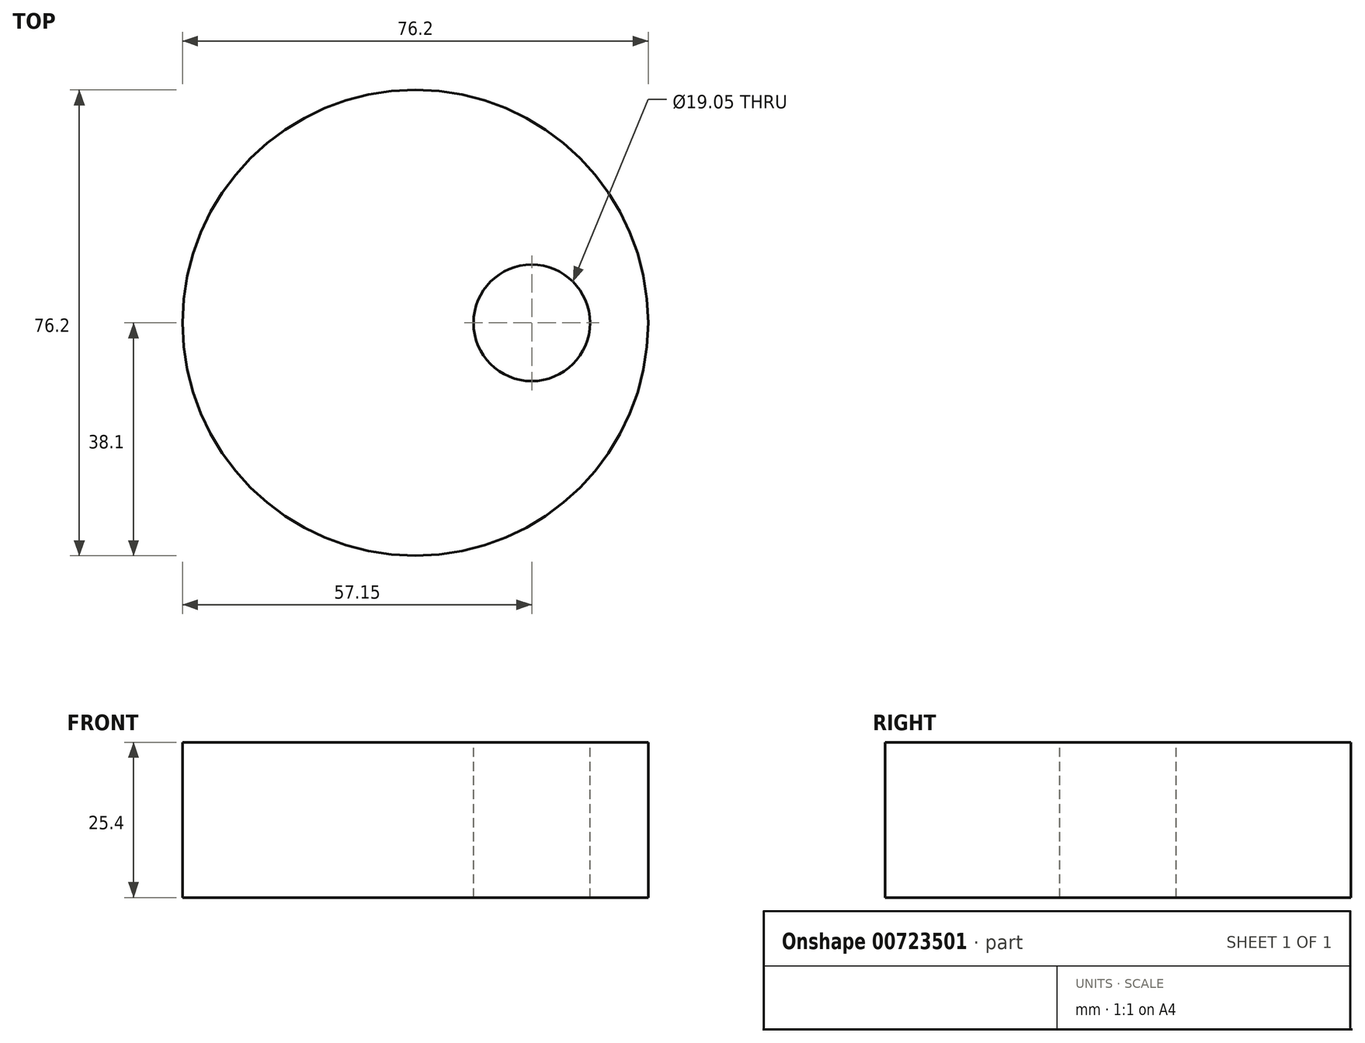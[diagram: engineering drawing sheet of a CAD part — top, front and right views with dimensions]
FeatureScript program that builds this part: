
annotation { "Feature Type Name" : "Feature", "Feature Type Description" : "" }
export const myFeature = defineFeature(function(context is Context, id is Id, definition is map)
    precondition{}
    {
        {
            var Q0;
            Q0=qCreatedBy(makeId("Top.planeOp"),FACE);
            var sketch = newSketch(context, id + "F0", { "sketchPlane" : qUnion([Q0])});
            skCircle(sketch, "E0", {"center": v(0, 0) * mm, "radius": 38.1 * mm});
            skSolve(sketch);
        }
        {
            var Q0;
            Q0=makeQuery(id+"F0.imprint","IMPRINT",FACE,{"disambiguationData":[TD([[makeQuery(id+"F0.imprint","IMPRINT",EDGE,{"derivedFrom":sQuery(id+"F0.wireOp",EDGE,"E0")}),1.0]])]});
            extrude(context, id + "F1", {"entities" : qUnion([Q0]), "depth" : 25.4 * mm, "offsetDistance" : 25.4 * mm});
        }
        {
            var Q0;
            Q0=makeQuery(id+"F1.opExtrude","CAP_FACE",FACE,{"disambiguationData":[OSD([sQuery(id+"F0.wireOp",EDGE,"E0")])],"isStart":false});
            var sketch = newSketch(context, id + "F2", { "sketchPlane" : qUnion([Q0])});
            skLineSegment(sketch, "E1", {"start": v(0, 0) * mm, "end": v(38.1, 0) * mm});
            skCircle(sketch, "E2", {"center": v(19.05, 0) * mm, "radius": 9.53 * mm});
            skSolve(sketch);
        }
        {
            var Q0;
            {var subQ0=sQuery(id+"F2.wireOp",EDGE,"E2");var subQ1=sQuery(id+"F2.wireOp",EDGE,"E1");var subQ2=makeQuery(id+"F2.imprint","INTERSECT",VERTEX,{"disambiguationData":[OD(0.0)],"derivedFrom":[subQ1,subQ0]});Q0=makeQuery(id+"F2.imprint","IMPRINT",FACE,{"disambiguationData":[TD([[makeQuery(id+"F2.imprint","IMPRINT",EDGE,{"disambiguationData":[TD([[subQ2,-1.0]])],"derivedFrom":subQ1}),-1.0]])]});}
            var Q1;
            {var subQ0=sQuery(id+"F2.wireOp",EDGE,"E2");var subQ1=sQuery(id+"F2.wireOp",EDGE,"E1");var subQ2=makeQuery(id+"F2.imprint","INTERSECT",VERTEX,{"disambiguationData":[OD(0.0)],"derivedFrom":[subQ1,subQ0]});Q1=makeQuery(id+"F2.imprint","IMPRINT",FACE,{"disambiguationData":[TD([[makeQuery(id+"F2.imprint","IMPRINT",EDGE,{"disambiguationData":[TD([[subQ2,-1.0]])],"derivedFrom":subQ1}),1.0]])]});}
            extrude(context, id + "F3", {"entities" : qUnion([Q0, Q1]), "operationType" : NewBodyOperationType.REMOVE, "oppositeDirection" : true, "depth" : 25.4 * mm, "offsetDistance" : 25.4 * mm});
        }
    });
